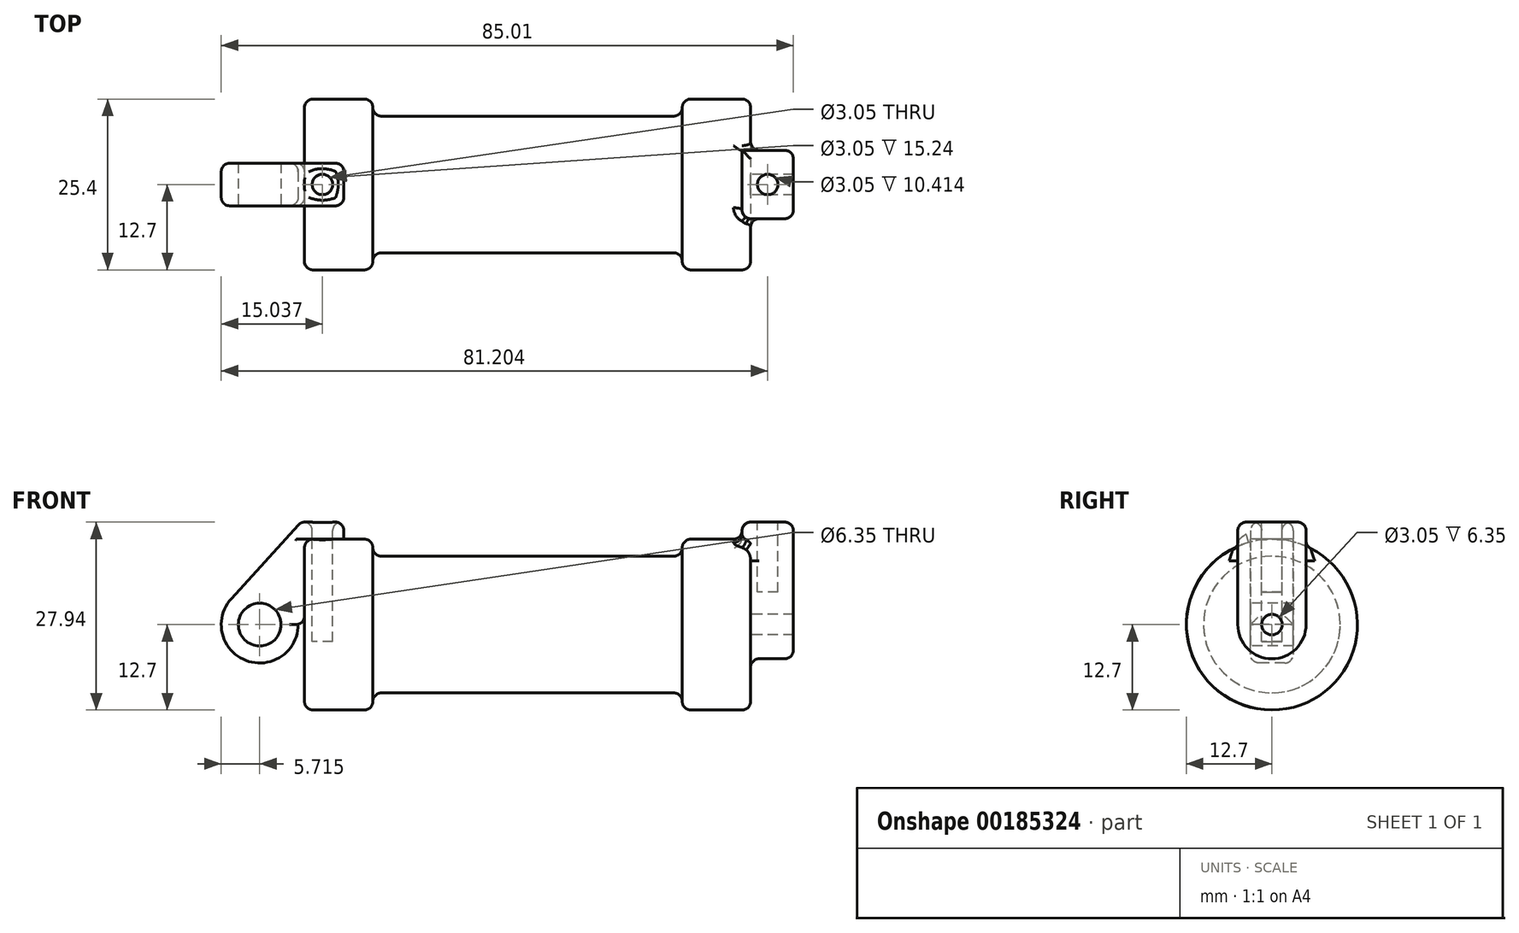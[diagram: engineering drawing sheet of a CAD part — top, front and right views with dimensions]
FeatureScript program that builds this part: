
annotation { "Feature Type Name" : "Feature", "Feature Type Description" : "" }
export const myFeature = defineFeature(function(context is Context, id is Id, definition is map)
    precondition{}
    {
        {
            var Q0;
            Q0=qCreatedBy(makeId("Front.planeOp"),FACE);
            var sketch = newSketch(context, id + "F0", { "sketchPlane" : qUnion([Q0])});
            skLineSegment(sketch, "E0", {"start": v(0, 0) * mm, "end": v(0, 12.7) * mm});
            skLineSegment(sketch, "E1", {"start": v(0, 12.7) * mm, "end": v(10.16, 12.7) * mm});
            skLineSegment(sketch, "E2", {"start": v(10.16, 12.7) * mm, "end": v(10.16, 10.16) * mm});
            skLineSegment(sketch, "E3", {"start": v(10.16, 10.16) * mm, "end": v(56.13, 10.16) * mm});
            skLineSegment(sketch, "E4", {"start": v(56.13, 10.16) * mm, "end": v(56.13, 12.7) * mm});
            skLineSegment(sketch, "E5", {"start": v(56.13, 12.7) * mm, "end": v(66.3, 12.7) * mm});
            skLineSegment(sketch, "E6", {"start": v(66.3, 12.7) * mm, "end": v(66.3, 0) * mm});
            skLineSegment(sketch, "E7", {"start": v(66.3, 0) * mm, "end": v(0, 0) * mm});
            skLineSegment(sketch, "E8", {"start": v(5.84, 15.24) * mm, "end": v(-0.5, 15.24) * mm});
            skLineSegment(sketch, "E9", {"start": v(-0.5, 15.24) * mm, "end": v(-10.88, 3.85) * mm});
            skLineSegment(sketch, "E10", {"start": v(0, 0) * mm, "end": v(-6.65, 0) * mm});
            skCircle(sketch, "E11", {"center": v(-6.65, 0) * mm, "radius": 5.72 * mm});
            skCircle(sketch, "E12", {"center": v(-6.65, 0) * mm, "radius": 3.18 * mm});
            skLineSegment(sketch, "E13", {"start": v(5.84, 15.24) * mm, "end": v(5.84, -9.4) * mm});
            skLineSegment(sketch, "E14", {"start": v(5.84, -9.4) * mm, "end": v(-8.18, -5.5) * mm});
            skSolve(sketch);
        }
        {
            var Q0;
            {var subQ0=sQuery(id+"F0.wireOp",EDGE,"E2");Q0=makeQuery(id+"F0.imprint","IMPRINT",FACE,{"disambiguationData":[TD([[makeQuery(id+"F0.imprint","IMPRINT",EDGE,{"derivedFrom":subQ0}),-1.0]])]});}
            var Q1;
            {var subQ0=sQuery(id+"F0.wireOp",EDGE,"E0");Q1=makeQuery(id+"F0.imprint","IMPRINT",FACE,{"disambiguationData":[TD([[makeQuery(id+"F0.imprint","IMPRINT",EDGE,{"derivedFrom":subQ0}),-1.0]])]});}
            var Q2;
            Q2=sQuery(id+"F0.wireOp",EDGE,"E7");
            revolve(context, id + "F1", {"entities" : qUnion([Q0, Q1]), "axis" : qUnion([Q2]), "revolveType" : RevolveType.FULL});
        }
        {
            var Q0;
            {var subQ3=sQuery(id+"F0.wireOp",EDGE,"E0");Q0=makeQuery(id+"F0.imprint","IMPRINT",FACE,{"disambiguationData":[TD([[makeQuery(id+"F0.imprint","IMPRINT",EDGE,{"derivedFrom":subQ3}),1.0]])]});}
            var Q1;
            {var subQ4=sQuery(id+"F0.wireOp",EDGE,"E12");Q1=makeQuery(id+"F0.imprint","IMPRINT",FACE,{"disambiguationData":[TD([[makeQuery(id+"F0.imprint","IMPRINT",EDGE,{"derivedFrom":subQ4}),-1.0]])]});}
            extrude(context, id + "F2", {"entities" : qUnion([Q0, Q1]), "endBound" : BoundingType.SYMMETRIC, "oppositeDirection" : true, "depth" : 6.35 * mm});
        }
        {
            var Q0;
            Q0=makeQuery(id+"F1.opRevolve","SWEPT_FACE",FACE,{"disambiguationData":[OSD([sQuery(id+"F0.wireOp",EDGE,"E6")])]});
            var sketch = newSketch(context, id + "F3", { "sketchPlane" : qUnion([Q0])});
            skCircle(sketch, "E15", {"center": v(0, 0) * mm, "radius": 1.52 * mm});
            skLineSegment(sketch, "E16", {"start": v(-5.08, 15.24) * mm, "end": v(-5.08, 0) * mm});
            skCircle(sketch, "E17", {"center": v(0, 0) * mm, "radius": 5.08 * mm});
            skLineSegment(sketch, "E18", {"start": v(5.08, 0) * mm, "end": v(5.08, 15.24) * mm});
            skLineSegment(sketch, "E19", {"start": v(5.08, 15.24) * mm, "end": v(-5.08, 15.24) * mm});
            skSolve(sketch);
        }
        {
            var Q0;
            Q0=makeQuery(id+"F3.imprint","IMPRINT",FACE,{"disambiguationData":[TD([[makeQuery(id+"F3.imprint","IMPRINT",EDGE,{"derivedFrom":sQuery(id+"F3.wireOp",EDGE,"E15")}),-1.0]])]});
            var Q1;
            {var subQ0=sQuery(id+"F3.wireOp",EDGE,"E17");var subQ1=sQuery(id+"F3.wireOp",EDGE,"E16");var subQ2=makeQuery(id+"F3.imprint","INTERSECT",VERTEX,{"derivedFrom":[subQ1,subQ0]});Q1=makeQuery(id+"F3.imprint","IMPRINT",FACE,{"disambiguationData":[TD([[makeQuery(id+"F3.imprint","IMPRINT",EDGE,{"disambiguationData":[TD([[subQ2,1.0]])],"derivedFrom":subQ0}),-1.0]])]});}
            var Q2;
            {var subQ0=sQuery(id+"F3.wireOp",EDGE,"E19");Q2=makeQuery(id+"F3.imprint","IMPRINT",FACE,{"disambiguationData":[TD([[makeQuery(id+"F3.imprint","IMPRINT",EDGE,{"derivedFrom":subQ0}),1.0]])]});}
            extrude(context, id + "F4", {"entities" : qUnion([Q0, Q1, Q2]), "operationType" : NewBodyOperationType.ADD, "depth" : 6.35 * mm, "hasSecondDirection" : true, "secondDirectionOppositeDirection" : true, "secondDirectionDepth" : 1.27 * mm});
        }
        {
            var Q0;
            Q0=makeQuery(id+"F4.boolean.opBoolean","SPLIT",FACE,{"disambiguationData":[TD([makeQuery(id+"F4.opExtrude","SWEPT_FACE",FACE,{"disambiguationData":[OSD([sQuery(id+"F3.wireOp",EDGE,"E15")])]})])],"derivedFrom":makeQuery(id+"F1.opRevolve","SWEPT_FACE",FACE,{"disambiguationData":[OSD([sQuery(id+"F0.wireOp",EDGE,"E6")])]})});
            extrude(context, id + "F5", {"entities" : qUnion([Q0]), "operationType" : NewBodyOperationType.ADD, "oppositeDirection" : true, "depth" : 1.27 * mm});
        }
        {
            var Q0;
            Q0=makeQuery(id+"F2.opExtrude","SWEPT_FACE",FACE,{"disambiguationData":[OSD([sQuery(id+"F0.wireOp",EDGE,"E8")])]});
            var sketch = newSketch(context, id + "F6", { "sketchPlane" : qUnion([Q0])});
            skCircle(sketch, "E20", {"center": v(2.67, 0) * mm, "radius": 1.52 * mm});
            skPoint(sketch, "E20.centerSnap0", {"position": v(2.67, 3.18) * mm});
            skPoint(sketch, "E20.centerSnap1", {"position": v(5.84, 0) * mm});
            skSolve(sketch);
        }
        {
            var Q0;
            Q0=makeQuery(id+"F4.opExtrude","SWEPT_FACE",FACE,{"disambiguationData":[OSD([sQuery(id+"F3.wireOp",EDGE,"E19")])]});
            var sketch = newSketch(context, id + "F7", { "sketchPlane" : qUnion([Q0])});
            skCircle(sketch, "E21", {"center": v(68.83, 0) * mm, "radius": 1.52 * mm});
            skPoint(sketch, "E21.centerSnap0", {"position": v(72.64, 0) * mm});
            skPoint(sketch, "E21.centerSnap1", {"position": v(68.83, 5.08) * mm});
            skSolve(sketch);
        }
        {
            var Q0;
            Q0=makeQuery(id+"F6.imprint","IMPRINT",FACE,{"disambiguationData":[TD([[makeQuery(id+"F6.imprint","IMPRINT",EDGE,{"derivedFrom":sQuery(id+"F6.wireOp",EDGE,"E20")}),1.0]])]});
            extrude(context, id + "F8", {"entities" : qUnion([Q0]), "operationType" : NewBodyOperationType.REMOVE, "oppositeDirection" : true, "depth" : 17.78 * mm});
        }
        {
            var Q0;
            Q0=makeQuery(id+"F7.imprint","IMPRINT",FACE,{"disambiguationData":[TD([[makeQuery(id+"F7.imprint","IMPRINT",EDGE,{"derivedFrom":sQuery(id+"F7.wireOp",EDGE,"E21")}),1.0]])]});
            extrude(context, id + "F9", {"entities" : qUnion([Q0]), "operationType" : NewBodyOperationType.REMOVE, "oppositeDirection" : true, "depth" : 10.4 * mm});
        }
        {
            var Q0;
            Q0=makeQuery(id+"F1.opRevolve","SWEPT_EDGE",EDGE,{"disambiguationData":[OSD([sQuery(id+"F0.wireOp",EDGE,"E4"),sQuery(id+"F0.wireOp",EDGE,"E5")])]});
            var Q1;
            Q1=makeQuery(id+"F1.opRevolve","SWEPT_EDGE",EDGE,{"disambiguationData":[OSD([sQuery(id+"F0.wireOp",EDGE,"E3"),sQuery(id+"F0.wireOp",EDGE,"E4")])]});
            var Q2;
            Q2=makeQuery(id+"F1.opRevolve","SWEPT_EDGE",EDGE,{"disambiguationData":[OSD([sQuery(id+"F0.wireOp",EDGE,"E1"),sQuery(id+"F0.wireOp",EDGE,"E2")])]});
            var Q3;
            Q3=makeQuery(id+"F1.opRevolve","SWEPT_EDGE",EDGE,{"disambiguationData":[OSD([sQuery(id+"F0.wireOp",EDGE,"E2"),sQuery(id+"F0.wireOp",EDGE,"E3")])]});
            var Q4;
            Q4=makeQuery(id+"F1.opRevolve","SWEPT_EDGE",EDGE,{"disambiguationData":[OSD([sQuery(id+"F0.wireOp",EDGE,"E0"),sQuery(id+"F0.wireOp",EDGE,"E1")])]});
            var Q5;
            Q5=makeQuery(id+"F1.opRevolve","SWEPT_EDGE",EDGE,{"disambiguationData":[OSD([sQuery(id+"F0.wireOp",EDGE,"E5"),sQuery(id+"F0.wireOp",EDGE,"E6")])]});
            fillet(context, id + "F10", {"entities" : qUnion([Q0, Q1, Q2, Q3, Q4, Q5]), "radius" : 1.27 * mm, "tangentPropagation" : true, "allowEdgeOverflow" : false});
        }
        {
            var Q0;
            Q0=makeQuery(id+"F4.opExtrude","CAP_EDGE",EDGE,{"disambiguationData":[OSD([sQuery(id+"F3.wireOp",EDGE,"E16")])],"isStart":true});
            var Q1;
            Q1=makeQuery(id+"F4.opExtrude","SWEPT_EDGE",EDGE,{"disambiguationData":[OSD([sQuery(id+"F3.wireOp",EDGE,"E16"),sQuery(id+"F3.wireOp",EDGE,"E19")])]});
            var Q2;
            Q2=makeQuery(id+"F4.opExtrude","CAP_EDGE",EDGE,{"disambiguationData":[OSD([sQuery(id+"F3.wireOp",EDGE,"E16")])],"isStart":false});
            var Q3;
            Q3=makeQuery(id+"F4.opExtrude","CAP_EDGE",EDGE,{"disambiguationData":[OSD([sQuery(id+"F3.wireOp",EDGE,"E17")])],"isStart":false});
            var Q4;
            Q4=makeQuery(id+"F4.opExtrude","CAP_EDGE",EDGE,{"disambiguationData":[OSD([sQuery(id+"F3.wireOp",EDGE,"E18")])],"isStart":false});
            var Q5;
            Q5=makeQuery(id+"F4.opExtrude","CAP_EDGE",EDGE,{"disambiguationData":[OSD([sQuery(id+"F3.wireOp",EDGE,"E19")])],"isStart":false});
            var Q6;
            Q6=makeQuery(id+"F4.opExtrude","CAP_EDGE",EDGE,{"disambiguationData":[OSD([sQuery(id+"F3.wireOp",EDGE,"E19")])],"isStart":true});
            var Q7;
            Q7=makeQuery(id+"F4.opExtrude","SWEPT_EDGE",EDGE,{"disambiguationData":[OSD([sQuery(id+"F3.wireOp",EDGE,"E18"),sQuery(id+"F3.wireOp",EDGE,"E19")])]});
            fillet(context, id + "F11", {"entities" : qUnion([Q0, Q1, Q2, Q3, Q4, Q5, Q6, Q7]), "radius" : 1.27 * mm, "tangentPropagation" : true, "allowEdgeOverflow" : false});
        }
        {
            var Q0;
            Q0=makeQuery(id+"F2.opExtrude","CAP_EDGE",EDGE,{"disambiguationData":[OSD([sQuery(id+"F0.wireOp",EDGE,"E9")])],"isStart":true});
            var Q1;
            Q1=makeQuery(id+"F2.opExtrude","CAP_EDGE",EDGE,{"disambiguationData":[OSD([sQuery(id+"F0.wireOp",EDGE,"E9")])],"isStart":false});
            var Q2;
            Q2=makeQuery(id+"F2.opExtrude","CAP_EDGE",EDGE,{"disambiguationData":[OSD([sQuery(id+"F0.wireOp",EDGE,"E8")])],"isStart":false});
            var Q3;
            Q3=makeQuery(id+"F2.opExtrude","CAP_EDGE",EDGE,{"disambiguationData":[OSD([sQuery(id+"F0.wireOp",EDGE,"E8")])],"isStart":true});
            var Q4;
            Q4=makeQuery(id+"F2.opExtrude","SWEPT_EDGE",EDGE,{"disambiguationData":[OSD([sQuery(id+"F0.wireOp",EDGE,"E8"),sQuery(id+"F0.wireOp",EDGE,"E13")])]});
            var Q5;
            Q5=makeQuery(id+"F2.opExtrude","SWEPT_FACE",FACE,{"disambiguationData":[OSD([sQuery(id+"F0.wireOp",EDGE,"E8")])]});
            var Q6;
            Q6=makeQuery(id+"F2.opExtrude","CAP_EDGE",EDGE,{"disambiguationData":[OSD([sQuery(id+"F0.wireOp",EDGE,"E11")])],"isStart":false});
            var Q7;
            Q7=makeQuery(id+"F2.opExtrude","CAP_EDGE",EDGE,{"disambiguationData":[OSD([sQuery(id+"F0.wireOp",EDGE,"E11")])],"isStart":true});
            fillet(context, id + "F12", {"entities" : qUnion([Q0, Q1, Q2, Q3, Q4, Q5, Q6, Q7]), "radius" : 1.27 * mm, "tangentPropagation" : true, "allowEdgeOverflow" : false});
        }
        {
            var Q0;
            Q0=makeQuery(id+"F2.opExtrude","CAP_EDGE",EDGE,{"disambiguationData":[OSD([sQuery(id+"F0.wireOp",EDGE,"E0")])],"isStart":true});
            var Q1;
            Q1=makeQuery(id+"F2.opExtrude","SWEPT_EDGE",EDGE,{"disambiguationData":[OSD([sQuery(id+"F0.wireOp",EDGE,"E0"),sQuery(id+"F0.wireOp",EDGE,"E7"),sQuery(id+"F0.wireOp",EDGE,"E10")])]});
            var Q2;
            Q2=makeQuery(id+"F2.opExtrude","CAP_EDGE",EDGE,{"disambiguationData":[OSD([sQuery(id+"F0.wireOp",EDGE,"E0")])],"isStart":false});
            var Q3;
            Q3=makeQuery(id+"F2.opExtrude","CAP_EDGE",EDGE,{"disambiguationData":[OSD([sQuery(id+"F0.wireOp",EDGE,"E13")])],"isStart":false});
            var Q4;
            Q4=makeQuery(id+"F2.opExtrude","CAP_EDGE",EDGE,{"disambiguationData":[OSD([sQuery(id+"F0.wireOp",EDGE,"E13")])],"isStart":true});
            fillet(context, id + "F13", {"entities" : qUnion([Q0, Q1, Q2, Q3, Q4]), "radius" : 1.27 * mm, "tangentPropagation" : true, "allowEdgeOverflow" : false});
        }
        {
            var Q0;
            Q0=makeQuery(id+"F4.boolean.opBoolean","INTERSECT",EDGE,{"derivedFrom":[makeQuery(id+"F1.opRevolve","SWEPT_FACE",FACE,{"disambiguationData":[OSD([sQuery(id+"F0.wireOp",EDGE,"E6")])]}),makeQuery(id+"F4.opExtrude","SWEPT_FACE",FACE,{"disambiguationData":[OSD([sQuery(id+"F3.wireOp",EDGE,"E18")])]})]});
            var Q1;
            Q1=makeQuery(id+"F4.boolean.opBoolean","INTERSECT",EDGE,{"derivedFrom":[makeQuery(id+"F1.opRevolve","SWEPT_FACE",FACE,{"disambiguationData":[OSD([sQuery(id+"F0.wireOp",EDGE,"E6")])]}),makeQuery(id+"F4.opExtrude","SWEPT_FACE",FACE,{"disambiguationData":[OSD([sQuery(id+"F3.wireOp",EDGE,"E16")])]})]});
            fillet(context, id + "F14", {"entities" : qUnion([Q0, Q1]), "radius" : 1.27 * mm, "tangentPropagation" : true, "allowEdgeOverflow" : false});
        }
    });
